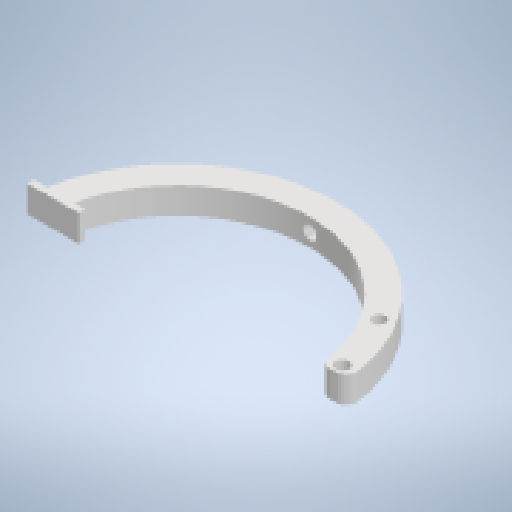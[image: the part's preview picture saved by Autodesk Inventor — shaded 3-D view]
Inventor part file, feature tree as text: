
AUTODESK INVENTOR PART (.ipt)
format: ipt  version: 2023 (Build 270158000, 158)  size: 282,112 bytes
history: native  units: mm
features: extrude x4, sketch x3, fillet x2
ambient origin geometry x8: Origin, YZ Plane, XZ Plane, XY Plane, X Axis, Y Axis, Z Axis, Center Point
bodies: Solido1 (feature_tree)
feature tree (9):
  sketch  "Schizzo1"
  extrude  "Estrusione1"  Depth=100.0mm
  extrude  "Estrusione2"  Depth=10.0mm TaperAngle=0.0deg
  fillet  "Raccordo3"  Radius=5.0mm
  fillet  "Raccordo4"  Radius=2.5mm
  extrude  "Estrusione3"  Depth=2.5mm
  extrude  "Estrusione5"  TaperAngle=0.0deg  [1 undecoded]
  sketch  "Schizzo2"
  sketch  "Schizzo4"
note: 1 required parameter value undecoded (feature->parameter linkage not recoverable at this tier; creation-order binding heuristic only, values carry confidence <= 0.55)
